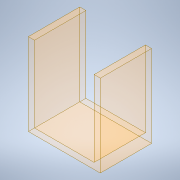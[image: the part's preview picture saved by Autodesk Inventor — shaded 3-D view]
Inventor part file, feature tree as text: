
AUTODESK INVENTOR PART (.ipt)
format: ipt  version: 2020 (Build 240168000, 168)  size: 103,424 bytes
history: native  units: mm
features: sketch x1, other x1, extrude x1
ambient origin geometry x8: Origin, YZ Plane, XZ Plane, XY Plane, X Axis, Y Axis, Z Axis, Center Point
bodies: Body1 (feature_tree)
feature tree (3):
  sketch  "Sketch1"  dims[d0=70.0mm d1=80.0mm d2=80.0mm d3=6.0mm d4=50.0mm d5=0.0mm]
  other  "Srf1"
  extrude  "ExtrusionSrf1"  Depth=80.0mm
